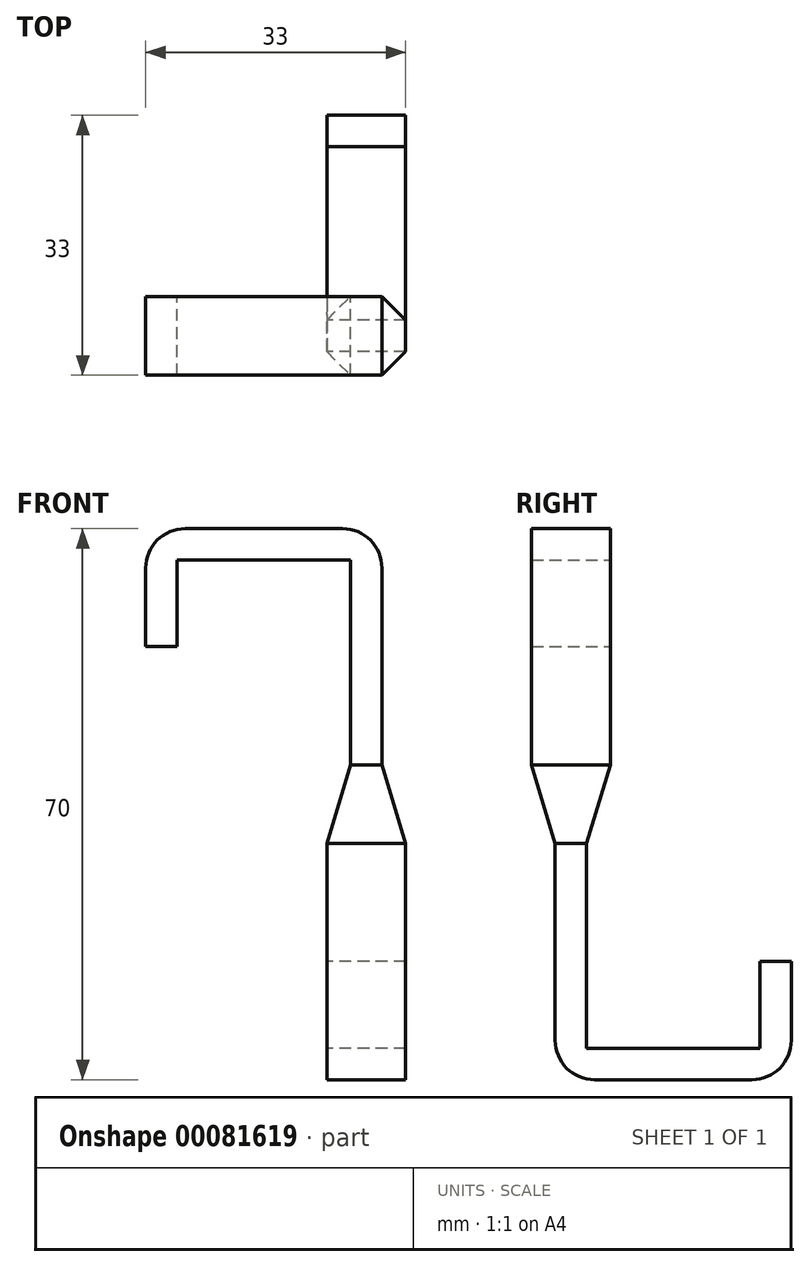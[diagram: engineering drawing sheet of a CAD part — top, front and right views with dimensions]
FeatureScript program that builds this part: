
annotation { "Feature Type Name" : "Feature", "Feature Type Description" : "" }
export const myFeature = defineFeature(function(context is Context, id is Id, definition is map)
    precondition{}
    {
        {
            var Q0;
            Q0=qCreatedBy(makeId("Front.planeOp"),FACE);
            var sketch = newSketch(context, id + "F0", { "sketchPlane" : qUnion([Q0])});
            skLineSegment(sketch, "E0", {"start": v(-53.05, 16.28) * mm, "end": v(-33.05, 16.28) * mm});
            skLineSegment(sketch, "E1", {"start": v(-58.05, 11.28) * mm, "end": v(-58.05, 1.28) * mm});
            skArc(sketch, "E2", {"start": v(-53.05, 16.28) * mm, "mid": v(-56.6, 14.81) * mm, "end": v(-58.05, 11.28) * mm});
            skLineSegment(sketch, "E3", {"start": v(-28.05, 11.28) * mm, "end": v(-28.05, -13.72) * mm});
            skArc(sketch, "E4", {"start": v(-28.05, 11.28) * mm, "mid": v(-29.52, 14.81) * mm, "end": v(-33.05, 16.28) * mm});
            skLineSegment(sketch, "E5.0", {"start": v(-32.05, 12.28) * mm, "end": v(-32.05, -13.72) * mm});
            skLineSegment(sketch, "E5.1", {"start": v(-54.05, 12.28) * mm, "end": v(-32.05, 12.28) * mm});
            skLineSegment(sketch, "E5.2", {"start": v(-54.05, 12.28) * mm, "end": v(-54.05, 1.28) * mm});
            skLineSegment(sketch, "E6", {"start": v(-58.05, 1.28) * mm, "end": v(-54.05, 1.28) * mm});
            skLineSegment(sketch, "E7", {"start": v(-32.05, -13.72) * mm, "end": v(-28.05, -13.72) * mm});
            skSolve(sketch);
        }
        {
            var Q0;
            Q0 = qSketchRegion(id + "F0", true);
            extrude(context, id + "F1", {"entities" : qUnion([Q0]), "depth" : 10 * mm});
        }
        {
            var Q0;
            Q0=makeQuery(id+"F1.opExtrude","SWEPT_BODY",BODY,{"disambiguationData":[OSD([sQuery(id+"F0.wireOp",EDGE,"E0"),sQuery(id+"F0.wireOp",EDGE,"E1"),sQuery(id+"F0.wireOp",EDGE,"E2"),sQuery(id+"F0.wireOp",EDGE,"E3"),sQuery(id+"F0.wireOp",EDGE,"E4"),sQuery(id+"F0.wireOp",EDGE,"E5.0"),sQuery(id+"F0.wireOp",EDGE,"E5.1"),sQuery(id+"F0.wireOp",EDGE,"E5.2"),sQuery(id+"F0.wireOp",EDGE,"E6"),sQuery(id+"F0.wireOp",EDGE,"E7")])]});
            var Q1;
            Q1=makeQuery(id+"F1.opExtrude","SWEPT_EDGE",EDGE,{"disambiguationData":[OSD([sQuery(id+"F0.wireOp",EDGE,"E3"),sQuery(id+"F0.wireOp",EDGE,"E7")])]});
            transform(context, id + "F2", {"entities" : qUnion([Q0]), "transformType" : TransformType.ROTATION, "transformAxis" : qUnion([Q1]), "angle" : 180 * degree, "makeCopy" : true});
        }
        {
            var Q0;
            Q0=makeQuery(id+"F2.opPattern","COPY",BODY,{"derivedFrom":makeQuery(id+"F1.opExtrude","SWEPT_BODY",BODY,{"disambiguationData":[OSD([sQuery(id+"F0.wireOp",EDGE,"E0"),sQuery(id+"F0.wireOp",EDGE,"E1"),sQuery(id+"F0.wireOp",EDGE,"E2"),sQuery(id+"F0.wireOp",EDGE,"E3"),sQuery(id+"F0.wireOp",EDGE,"E4"),sQuery(id+"F0.wireOp",EDGE,"E5.0"),sQuery(id+"F0.wireOp",EDGE,"E5.1"),sQuery(id+"F0.wireOp",EDGE,"E5.2"),sQuery(id+"F0.wireOp",EDGE,"E6"),sQuery(id+"F0.wireOp",EDGE,"E7")])]}),"instanceName":"1"});
            var Q1;
            Q1=makeQuery(id+"F2.opPattern","COPY",EDGE,{"derivedFrom":makeQuery(id+"F1.opExtrude","CAP_EDGE",EDGE,{"disambiguationData":[OSD([sQuery(id+"F0.wireOp",EDGE,"E3")])],"isStart":true}),"instanceName":"1"});
            transform(context, id + "F3", {"entities" : qUnion([Q0]), "transformType" : TransformType.ROTATION, "transformAxis" : qUnion([Q1]), "angle" : 90 * degree, "makeCopy" : false});
        }
        {
            var Q0;
            Q0=makeQuery(id+"F2.opPattern","COPY",BODY,{"derivedFrom":makeQuery(id+"F1.opExtrude","SWEPT_BODY",BODY,{"disambiguationData":[OSD([sQuery(id+"F0.wireOp",EDGE,"E0"),sQuery(id+"F0.wireOp",EDGE,"E1"),sQuery(id+"F0.wireOp",EDGE,"E2"),sQuery(id+"F0.wireOp",EDGE,"E3"),sQuery(id+"F0.wireOp",EDGE,"E4"),sQuery(id+"F0.wireOp",EDGE,"E5.0"),sQuery(id+"F0.wireOp",EDGE,"E5.1"),sQuery(id+"F0.wireOp",EDGE,"E5.2"),sQuery(id+"F0.wireOp",EDGE,"E6"),sQuery(id+"F0.wireOp",EDGE,"E7")])]}),"instanceName":"1"});
            transform(context, id + "F4", {"entities" : qUnion([Q0]), "transformType" : TransformType.TRANSLATION_3D, "dx" : -7 * mm, "dy" : -7 * mm, "dz" : -10 * mm, "makeCopy" : false});
        }
        {
            var Q1;
            Q1=makeQuery(id+"F2.opPattern","COPY",FACE,{"derivedFrom":makeQuery(id+"F1.opExtrude","SWEPT_FACE",FACE,{"disambiguationData":[OSD([sQuery(id+"F0.wireOp",EDGE,"E7")])]}),"instanceName":"1"});
            var Q2;
            Q2=makeQuery(id+"F1.opExtrude","SWEPT_FACE",FACE,{"disambiguationData":[OSD([sQuery(id+"F0.wireOp",EDGE,"E7")])]});
            loft(context, id + "F5", {"operationType" : NewBodyOperationType.ADD, "sheetProfilesArray" : [{ "sheetProfileEntities" : qUnion([Q1]) }, { "sheetProfileEntities" : qUnion([Q2]) }]});
        }
    });
